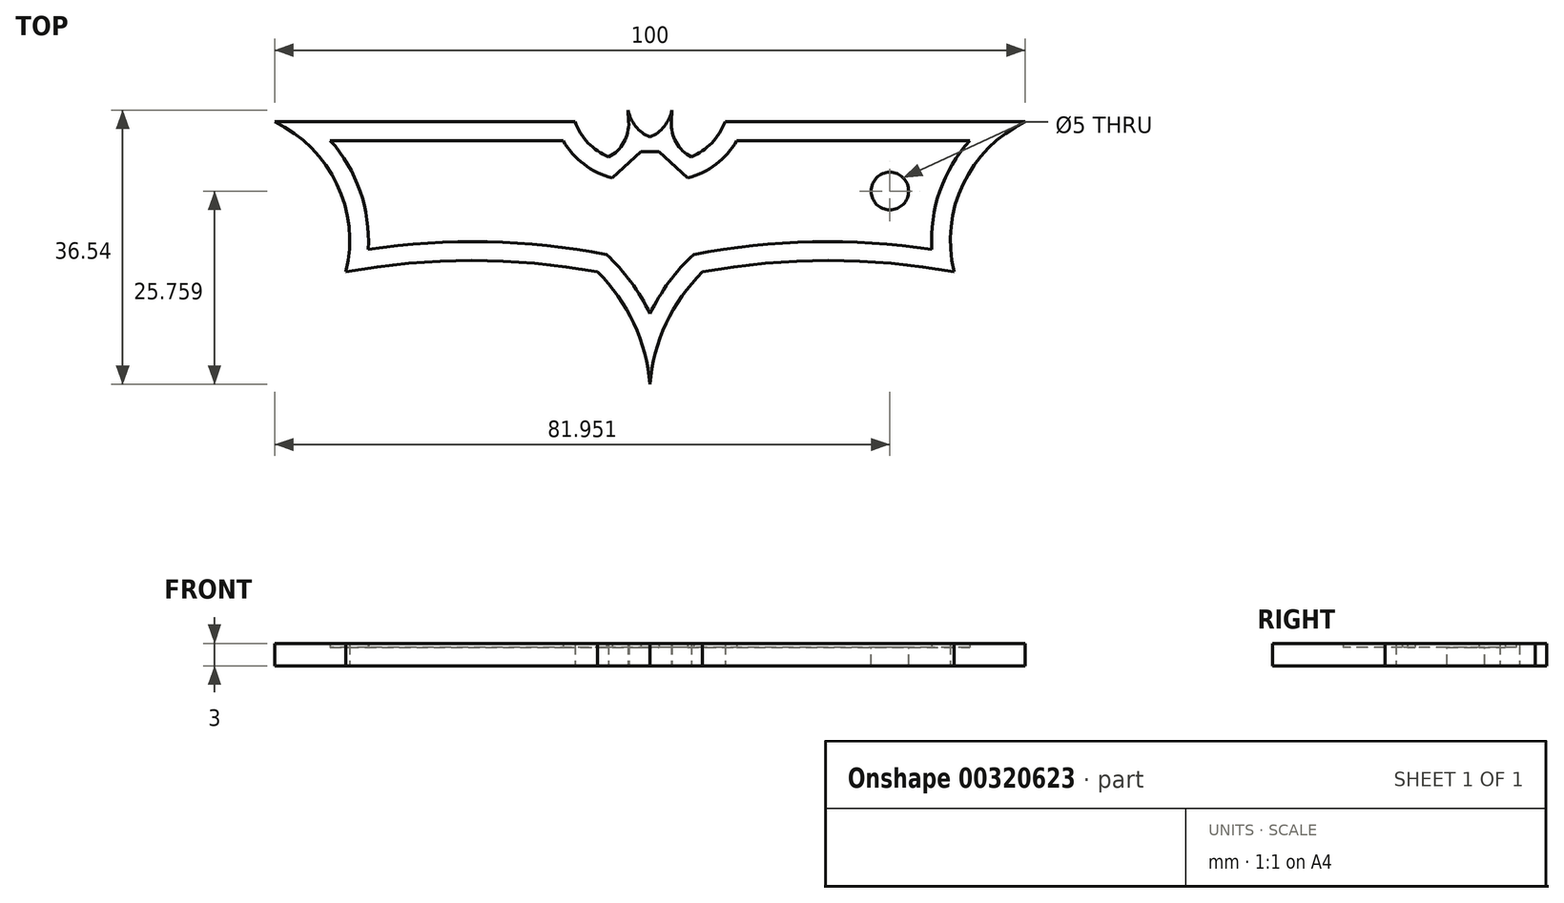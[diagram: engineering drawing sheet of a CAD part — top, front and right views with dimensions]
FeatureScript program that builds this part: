
annotation { "Feature Type Name" : "Feature", "Feature Type Description" : "" }
export const myFeature = defineFeature(function(context is Context, id is Id, definition is map)
    precondition{}
    {
        {
            var Q0;
            Q0=qCreatedBy(makeId("Top.planeOp"),FACE);
            var sketch = newSketch(context, id + "F0", { "sketchPlane" : qUnion([Q0])});
            skLineSegment(sketch, "E0", {"start": v(-50, 15) * mm, "end": v(-10, 15) * mm});
            skArc(sketch, "E1", {"start": v(-40.5, -5) * mm, "mid": v(-41.7, 6.69) * mm, "end": v(-50, 15) * mm});
            skArc(sketch, "E2", {"start": v(0, -20) * mm, "mid": v(-2.16, -11.87) * mm, "end": v(-7, -5) * mm});
            skArc(sketch, "E3.MirrorCS", {"start": v(0, -20) * mm, "mid": v(2.16, -11.87) * mm, "end": v(7, -5) * mm});
            skArc(sketch, "E4.MirrorCS", {"start": v(40.5, -5) * mm, "mid": v(41.7, 6.69) * mm, "end": v(50, 15) * mm});
            skArc(sketch, "E5", {"start": v(-10, 15) * mm, "mid": v(-8.24, 12.18) * mm, "end": v(-5.5, 10.3) * mm});
            skArc(sketch, "E6.MirrorCS", {"start": v(10, 15) * mm, "mid": v(8.24, 12.18) * mm, "end": v(5.5, 10.3) * mm});
            skPoint(sketch, "E7.orphan", {"position": v(40.5, -5) * mm});
            skArc(sketch, "E8", {"start": v(-7, -5) * mm, "mid": v(-23.75, -3.5) * mm, "end": v(-40.5, -5) * mm});
            skArc(sketch, "E9.MirrorCS", {"start": v(7, -5) * mm, "mid": v(23.75, -3.5) * mm, "end": v(40.5, -5) * mm});
            skArc(sketch, "E10", {"start": v(-3, 18) * mm, "mid": v(-2.32, 14.99) * mm, "end": v(0, 12.95) * mm});
            skLineSegment(sketch, "E11", {"start": v(-3, 18) * mm, "end": v(-2.84, 15) * mm});
            skArc(sketch, "E12.MirrorCS", {"start": v(3, 18) * mm, "mid": v(2.32, 14.99) * mm, "end": v(0, 12.95) * mm});
            skLineSegment(sketch, "E13.MirrorCS", {"start": v(3, 18) * mm, "end": v(2.84, 15) * mm});
            skPoint(sketch, "E14.start.orphan", {"position": v(-3, 9.91) * mm});
            skArc(sketch, "E15", {"start": v(-5.5, 10.3) * mm, "mid": v(-3.48, 12.26) * mm, "end": v(-2.84, 15) * mm});
            skArc(sketch, "E16.MirrorCS", {"start": v(5.5, 10.3) * mm, "mid": v(3.48, 12.26) * mm, "end": v(2.84, 15) * mm});
            skPoint(sketch, "E17.trimOffspring.end.orphan", {"position": v(0, 10) * mm});
            skLineSegment(sketch, "E18.trimOffspring", {"start": v(10, 15) * mm, "end": v(50, 15) * mm});
            skLineSegment(sketch, "E19.trimOffspring", {"start": v(2.33, 15) * mm, "end": v(2.33, 15) * mm});
            skPoint(sketch, "E20.orphan", {"position": v(-4.98, -20) * mm});
            skPoint(sketch, "E21.end.orphan", {"position": v(4.98, -20) * mm});
            skLineSegment(sketch, "E22.trimOffspring", {"start": v(-2.33, 15) * mm, "end": v(-2.33, 15) * mm});
            skSolve(sketch);
        }
        {
            var Q0;
            {var subQ8=sQuery(id+"F0.wireOp",EDGE,"E1");Q0=makeQuery(id+"F0.imprint","IMPRINT",FACE,{"disambiguationData":[TD([[makeQuery(id+"F0.imprint","IMPRINT",EDGE,{"derivedFrom":subQ8}),-1.0]])]});}
            var sketch = newSketch(context, id + "F1", { "sketchPlane" : qUnion([Q0])});
            skArc(sketch, "E23.1", {"start": v(5.81, -2.68) * mm, "mid": v(21.64, -1.02) * mm, "end": v(37.53, -1.99) * mm});
            skArc(sketch, "E23.2", {"start": v(37.53, -1.99) * mm, "mid": v(38.62, 5.76) * mm, "end": v(42.58, 12.5) * mm});
            skLineSegment(sketch, "E23.3", {"start": v(11.58, 12.5) * mm, "end": v(42.58, 12.5) * mm});
            skArc(sketch, "E23.4", {"start": v(11.58, 12.5) * mm, "mid": v(8.8, 9.34) * mm, "end": v(5, 7.5) * mm});
            skArc(sketch, "E23.5", {"start": v(0, -10.58) * mm, "mid": v(2.53, -6.36) * mm, "end": v(5.81, -2.68) * mm});
            skArc(sketch, "E23.6", {"start": v(0, -10.58) * mm, "mid": v(-2.53, -6.36) * mm, "end": v(-5.81, -2.68) * mm});
            skArc(sketch, "E23.7", {"start": v(-5.81, -2.68) * mm, "mid": v(-21.64, -1.02) * mm, "end": v(-37.53, -1.99) * mm});
            skArc(sketch, "E23.8", {"start": v(-37.53, -1.99) * mm, "mid": v(-38.62, 5.76) * mm, "end": v(-42.58, 12.5) * mm});
            skLineSegment(sketch, "E23.9", {"start": v(-42.58, 12.5) * mm, "end": v(-11.58, 12.5) * mm});
            skArc(sketch, "E23.10", {"start": v(-11.58, 12.5) * mm, "mid": v(-8.8, 9.34) * mm, "end": v(-5, 7.5) * mm});
            skLineSegment(sketch, "E24", {"start": v(-5, 7.5) * mm, "end": v(-1.22, 11) * mm});
            skLineSegment(sketch, "E25.MirrorCS", {"start": v(5, 7.5) * mm, "end": v(1.22, 11) * mm});
            skLineSegment(sketch, "E26", {"start": v(-1.22, 11) * mm, "end": v(1.22, 11) * mm});
            skSolve(sketch);
        }
        {
            var Q0;
            Q0=makeQuery(id+"F1.imprint","IMPRINT",FACE,{"disambiguationData":[TD([[makeQuery(id+"F1.imprint","IMPRINT",EDGE,{"derivedFrom":sQuery(id+"F1.wireOp",EDGE,"E23.1")}),1.0]])]});
            extrude(context, id + "F2", {"entities" : qUnion([Q0]), "depth" : 3 * mm});
        }
        {
            var Q0;
            Q0=makeQuery(id+"F0.imprint","IMPRINT",FACE,{"disambiguationData":[TD([[makeQuery(id+"F0.imprint","IMPRINT",EDGE,{"derivedFrom":sQuery(id+"F0.wireOp",EDGE,"E0")}),-1.0]])]});
            extrude(context, id + "F3", {"entities" : qUnion([Q0]), "operationType" : NewBodyOperationType.ADD, "depth" : 2.5 * mm});
        }
        {
            var Q0;
            Q0=makeQuery(id+"F2.opExtrude","CAP_FACE",FACE,{"disambiguationData":[OSD([sQuery(id+"F1.wireOp",EDGE,"E23.1"),sQuery(id+"F1.wireOp",EDGE,"E23.2"),sQuery(id+"F1.wireOp",EDGE,"E23.3"),sQuery(id+"F1.wireOp",EDGE,"E23.4"),sQuery(id+"F1.wireOp",EDGE,"E23.5"),sQuery(id+"F1.wireOp",EDGE,"E23.6"),sQuery(id+"F1.wireOp",EDGE,"E23.7"),sQuery(id+"F1.wireOp",EDGE,"E23.8"),sQuery(id+"F1.wireOp",EDGE,"E23.9"),sQuery(id+"F1.wireOp",EDGE,"E23.10"),sQuery(id+"F1.wireOp",EDGE,"E24"),sQuery(id+"F1.wireOp",EDGE,"E25.MirrorCS"),sQuery(id+"F1.wireOp",EDGE,"E26")])],"isStart":false});
            var sketch = newSketch(context, id + "F4", { "sketchPlane" : qUnion([Q0])});
            skPoint(sketch, "E27", {"position": v(31.95, 5.76) * mm});
            skPoint(sketch, "E27.positionSnap0", {"position": v(38.62, 5.76) * mm});
            skSolve(sketch);
        }
        {
            var Q0;
            Q0=sQuery(id+"F4.wireOp",VERTEX,"E27");
            var Q1;
            Q1=makeQuery(id+"F2.opExtrude","SWEPT_BODY",BODY,{"disambiguationData":[OSD([sQuery(id+"F1.wireOp",EDGE,"E23.1"),sQuery(id+"F1.wireOp",EDGE,"E23.2"),sQuery(id+"F1.wireOp",EDGE,"E23.3"),sQuery(id+"F1.wireOp",EDGE,"E23.4"),sQuery(id+"F1.wireOp",EDGE,"E23.5"),sQuery(id+"F1.wireOp",EDGE,"E23.6"),sQuery(id+"F1.wireOp",EDGE,"E23.7"),sQuery(id+"F1.wireOp",EDGE,"E23.8"),sQuery(id+"F1.wireOp",EDGE,"E23.9"),sQuery(id+"F1.wireOp",EDGE,"E23.10"),sQuery(id+"F1.wireOp",EDGE,"E24"),sQuery(id+"F1.wireOp",EDGE,"E25.MirrorCS"),sQuery(id+"F1.wireOp",EDGE,"E26")])]});
            hole(context, id + "F5", {"style" : HoleStyle.SIMPLE, "endStyle" : HoleEndStyle.BLIND, "holeDiameter" : 5 * mm, "holeDepth" : 300 * mm, "tappedDepth" : 12 * mm, "tapClearance" : 3, "locations" : qUnion([Q0]), "scope" : qUnion([Q1])});
        }
    });
